# Revit family: 9af5c458-e024-4ac5-85c6-063342da6070
name_source: partatom
category: Site
revit_build: Autodesk Revit 2016 (Build: 20161004_0715(x64)
units: mm (PartAtom-declared; Revit-internal decimal feet)

## family parameters
Always vertical = Yes
Cut with Voids When Loaded = No
Part Type = Normal
Round Connector Dimension = Use Diameter
Shared = No
Work Plane-Based = No

## types (2) — shared parameters
Depth = 145 11/16"
Description = Ashlar Pattern Guide
Manufacturer = Stepstone, Inc.
Manufacturer Fax = 310.217.1424
Model = Ashlar Pattern
Product Page URL = http://www.stepstoneinc.com
Revit Object Download Link = http://library.smartbim.com
Subcategory = CalArc Pavers
Surface Finish = Integral
Type Image = <None>
URL = stepstoneinc.com
Width = 133 7/32"

## per-type parameters (varying)
| type | Paver A Pattern | Paver B Pattern |
| 1800 Color Option 1 | Concrete - Stepstone - French1804 | Concrete - Stepstone - Porcelain1813 |
| 1400 Color Option 1 | Concrete - Stepstone - French1404 | Concrete - Stepstone - Porcelain1413 |

## geometry (parser evidence)
native form markers: Blend x10, Sweep x27
no freeform markers — native parametric forms only
